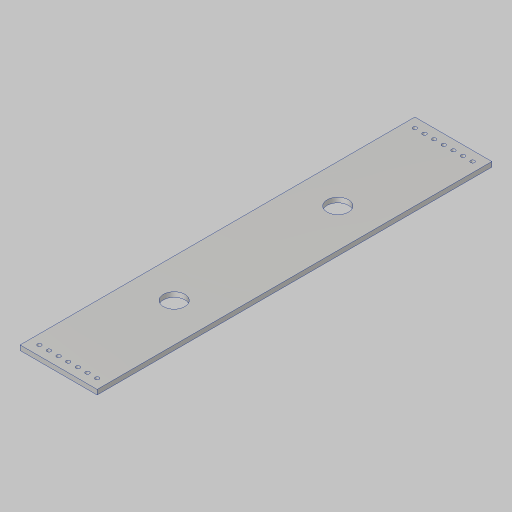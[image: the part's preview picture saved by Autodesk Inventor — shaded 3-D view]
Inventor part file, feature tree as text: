
AUTODESK INVENTOR PART (.ipt)
format: ipt  version: 2023.5 (Build 275446000, 446)  size: 124,416 bytes
history: native  units: in
note: dims shown in document units (in); Inventor stores cm internally (conversion verified against a paired STEP export)
features: sketch x3, extrude x2, hole x1
ambient origin geometry x8: Origin, YZ Plane, XZ Plane, XY Plane, X Axis, Y Axis, Z Axis, Center Point
bodies: Solid1 (feature_tree)
feature tree (6):
  extrude  "Extrusion1"  Depth=20.5in
  extrude  "Extrusion2"  Depth=0.25in
  hole  "Hole1"  [1 undecoded]
  sketch  "Sketch1"  dims[d0=4.0in d1=20.5in]
  sketch  "Sketch2"  dims[d2=0.25in d3=0.0in d5=1.11in]
  sketch  "Sketch3"  dims[d7=5.0in d8=5.0in d9=3.5in d10=4.5in d12=6.0039in d13=0.25in d14=0.0in d15=0.5in d16=0.5in d17=2.7559in d19=0.5in d20=0.3937in d22=1.0in d24=0.201in d25=0.75in d26=0.385in d27=0.25in d28=0.5635in d29=1.0in d30=0.8108in]
note: 1 required parameter value undecoded (feature->parameter linkage not recoverable at this tier; creation-order binding heuristic only, values carry confidence <= 0.55)
